FCSTD DOCUMENT  (FreeCAD 0.18R16146 (Git))
Label: 1
License: All rights reserved
LicenseURL: http://en.wikipedia.org/wiki/All_rights_reserved
objects: Sketcher::SketchObject×4
note: 4 computed .brp shape members not serialized (recipe doc carries the construction recipe); baked Part::Feature solids carry a one-line shape summary decoded from their .brp

FEATURE [Sketcher::SketchObject] Sketch001  label="Base"
  sketch-geometry (14):
    g0: LineSegment StartX=-17 StartY=19 StartZ=0 EndX=17 EndY=19 EndZ=0
    g1: LineSegment StartX=17 StartY=19 StartZ=0 EndX=17 EndY=-19 EndZ=0
    g2: LineSegment StartX=17 StartY=-19 StartZ=0 EndX=-17 EndY=-19 EndZ=0
    g3: LineSegment StartX=-17 StartY=-19 StartZ=0 EndX=-17 EndY=19 EndZ=0
    g4: LineSegment StartX=-11.5 StartY=6.5 StartZ=0 EndX=11.5 EndY=6.5 EndZ=0
    g5: LineSegment StartX=11.5 StartY=6.5 StartZ=0 EndX=11.5 EndY=-6.5 EndZ=0
    g6: LineSegment StartX=11.5 StartY=-6.5 StartZ=0 EndX=-11.5 EndY=-6.5 EndZ=0
    g7: LineSegment StartX=-11.5 StartY=-6.5 StartZ=0 EndX=-11.5 EndY=6.5 EndZ=0
    g8: Circle CenterX=13.5451 CenterY=-0.027259 CenterZ=0 NormalX=0 NormalY=0 NormalZ=1 AngleXU=0 Radius=1.48896
    g9: Circle CenterX=-13.4593 CenterY=-0.048301 CenterZ=0 NormalX=0 NormalY=0 NormalZ=1 AngleXU=0 Radius=1.52897
    g10: Circle CenterX=14.0269 CenterY=16.0422 CenterZ=0 NormalX=0 NormalY=0 NormalZ=1 AngleXU=0 Radius=1.46402
    g11: Circle CenterX=-14.0231 CenterY=16.0229 CenterZ=0 NormalX=0 NormalY=0 NormalZ=1 AngleXU=0 Radius=1.51917
    g12: Circle CenterX=-13.979 CenterY=-15.9717 CenterZ=0 NormalX=0 NormalY=0 NormalZ=1 AngleXU=0 Radius=1.45797
    g13: Circle CenterX=13.996 CenterY=-16.009 CenterZ=0 NormalX=0 NormalY=0 NormalZ=1 AngleXU=0 Radius=1.48678
  constraints (19):
    c: Coincident(g0,g1)
    c: Coincident(g1,g2)
    c: Coincident(g2,g3)
    c: Coincident(g3,g0)
    c: Vertical(g3)
    c: DistanceX(g0,g0) = 34
    c: DistanceY(g1,g1) = 38
    c: Symmetric(g1,g0,g-1)
    c: Symmetric(g2,g1,g-2)
    c: Horizontal(g0)
    c: Coincident(g4,g5)
    c: Coincident(g5,g6)
    c: Coincident(g6,g7)
    c: Coincident(g7,g4)
    c: Vertical(g7)
    c: DistanceX(g6,g6) = 23
    c: DistanceY(g5,g5) = 13
    c: Symmetric(g5,g4,g-1)
    c: Symmetric(g4,g4,g-2)
FEATURE [Sketcher::SketchObject] Sketch002  label="Second servo base"
  sketch-geometry (5):
    g0: LineSegment StartX=-17 StartY=19 StartZ=0 EndX=17 EndY=19 EndZ=0
    g1: LineSegment StartX=17 StartY=19 StartZ=0 EndX=17 EndY=-19 EndZ=0
    g2: LineSegment StartX=17 StartY=-19 StartZ=0 EndX=-17 EndY=-19 EndZ=0
    g3: LineSegment StartX=-17 StartY=-19 StartZ=0 EndX=-17 EndY=19 EndZ=0
    g4: Circle CenterX=-0.0018 CenterY=-0.022057 CenterZ=0 NormalX=0 NormalY=0 NormalZ=1 AngleXU=0 Radius=0.98284
  constraints (10):
    c: Coincident(g0,g1)
    c: Coincident(g1,g2)
    c: Coincident(g2,g3)
    c: Coincident(g3,g0)
    c: Vertical(g3)
    c: DistanceX(g0,g0) = 34
    c: DistanceY(g1,g1) = 38
    c: Symmetric(g1,g0,g-1)
    c: Symmetric(g2,g1,g-2)
    c: Horizontal(g0)
FEATURE [Sketcher::SketchObject] Sketch  label="Arm Holder"
  sketch-geometry (10):
    g0: LineSegment StartX=-15.5 StartY=25 StartZ=0 EndX=15.5 EndY=25 EndZ=0
    g1: LineSegment StartX=15.5 StartY=25 StartZ=0 EndX=15.5 EndY=-25 EndZ=0
    g2: LineSegment StartX=15.5 StartY=-25 StartZ=0 EndX=-14.9873 EndY=-24.9793 EndZ=0
    g3: LineSegment StartX=-14.9873 StartY=-24.9793 StartZ=0 EndX=-15.5 EndY=25 EndZ=0
    g4: Circle CenterX=-0.010938 CenterY=7.45508 CenterZ=0 NormalX=0 NormalY=0 NormalZ=1 AngleXU=0 Radius=1
    g5: Circle CenterX=0.003591 CenterY=-16.2778 CenterZ=0 NormalX=0 NormalY=0 NormalZ=1 AngleXU=0 Radius=2
    g6: LineSegment StartX=-10.0082 StartY=2.5419 StartZ=0 EndX=9.98924 EndY=2.5419 EndZ=0
    g7: LineSegment StartX=9.98924 StartY=2.5419 StartZ=0 EndX=9.98924 EndY=-5.9476 EndZ=0
    g8: LineSegment StartX=9.98924 StartY=-5.9476 StartZ=0 EndX=-10.0082 EndY=-5.9476 EndZ=0
    g9: LineSegment StartX=-10.0082 StartY=-5.9476 StartZ=0 EndX=-10.0082 EndY=2.5419 EndZ=0
  constraints (18):
    c: Coincident(g0,g1)
    c: Coincident(g1,g2)
    c: Coincident(g2,g3)
    c: Coincident(g3,g0)
    c: Symmetric(g1,g0,g-1)
    c: Symmetric(g0,g0,g-2)
    c: DistanceX(g0,g0) = 31
    c: DistanceY(g1,g1) = 50
    c: Coincident(g6,g7)
    c: Coincident(g7,g8)
    c: Coincident(g8,g9)
    c: Coincident(g9,g6)
    c: Horizontal(g6)
    c: Horizontal(g8)
    c: Vertical(g7)
    c: Vertical(g9)
    c: Radius(g5) = 2
    c: Radius(g4) = 1
FEATURE [Sketcher::SketchObject] Sketch003  label="Platform"
  sketch-geometry (17):
    g0: LineSegment StartX=-40 StartY=15.5 StartZ=0 EndX=40 EndY=15.5 EndZ=0
    g1: LineSegment StartX=40 StartY=15.5 StartZ=0 EndX=40 EndY=-15.5 EndZ=0
    g2: LineSegment StartX=40 StartY=-15.5 StartZ=0 EndX=-40 EndY=-15.5 EndZ=0
    g3: LineSegment StartX=-40 StartY=-15.5 StartZ=0 EndX=-40 EndY=15.5 EndZ=0
    g4: LineSegment StartX=-10.0082 StartY=2.5419 StartZ=0 EndX=9.98924 EndY=2.5419 EndZ=0
    g5: LineSegment StartX=9.98924 StartY=2.5419 StartZ=0 EndX=9.98924 EndY=-5.9476 EndZ=0
    g6: LineSegment StartX=9.98924 StartY=-5.9476 StartZ=0 EndX=-10.0082 EndY=-5.9476 EndZ=0
    g7: LineSegment StartX=-10.0082 StartY=-5.9476 StartZ=0 EndX=-10.0082 EndY=2.5419 EndZ=0
    g8: Circle CenterX=-31.3416 CenterY=-0.042606 CenterZ=0 NormalX=0 NormalY=0 NormalZ=1 AngleXU=0 Radius=1.95308
    g9: Circle CenterX=-36.459 CenterY=13.0048 CenterZ=0 NormalX=0 NormalY=0 NormalZ=1 AngleXU=0 Radius=1.5
    g10: Circle CenterX=-36.4614 CenterY=-12.9727 CenterZ=0 NormalX=0 NormalY=0 NormalZ=1 AngleXU=0 Radius=1.5
    g11: Circle CenterX=-11.462 CenterY=12.9712 CenterZ=0 NormalX=0 NormalY=0 NormalZ=1 AngleXU=0 Radius=1.5
    g12: Circle CenterX=-11.4615 CenterY=-12.9704 CenterZ=0 NormalX=0 NormalY=0 NormalZ=1 AngleXU=0 Radius=1.5
    g13: Circle CenterX=10.5013 CenterY=13.0214 CenterZ=0 NormalX=0 NormalY=0 NormalZ=1 AngleXU=0 Radius=1.5
    g14: Circle CenterX=10.4989 CenterY=-12.9561 CenterZ=0 NormalX=0 NormalY=0 NormalZ=1 AngleXU=0 Radius=1.5
    g15: Circle CenterX=35.4988 CenterY=-12.9539 CenterZ=0 NormalX=0 NormalY=0 NormalZ=1 AngleXU=0 Radius=1.5
    g16: Circle CenterX=36.4795 CenterY=13.001 CenterZ=0 NormalX=0 NormalY=0 NormalZ=1 AngleXU=0 Radius=1.5
  constraints (25):
    c: Coincident(g0,g1)
    c: Coincident(g1,g2)
    c: Coincident(g2,g3)
    c: Coincident(g3,g0)
    c: Symmetric(g1,g0,g-1)
    c: Symmetric(g0,g0,g-2)
    c: DistanceX(g0,g0) = 80
    c: DistanceY(g1,g1) = 31
    c: Coincident(g4,g5)
    c: Coincident(g5,g6)
    c: Coincident(g6,g7)
    c: Coincident(g7,g4)
    c: Horizontal(g4)
    c: Horizontal(g6)
    c: Vertical(g5)
    c: Vertical(g7)
    c: Symmetric(g2,g0,g-1)
    c: Radius(g9) = 1.5
    c: Equal(g9,g10) = 1.5
    c: Equal(g9,g11) = 1.5
    c: Equal(g11,g12) = 1.5
    c: Equal(g9,g13) = 1.5
    c: Equal(g13,g14) = 1.5
    c: Equal(g13,g16) = 1.5
    c: Equal(g16,g15) = 1.5
